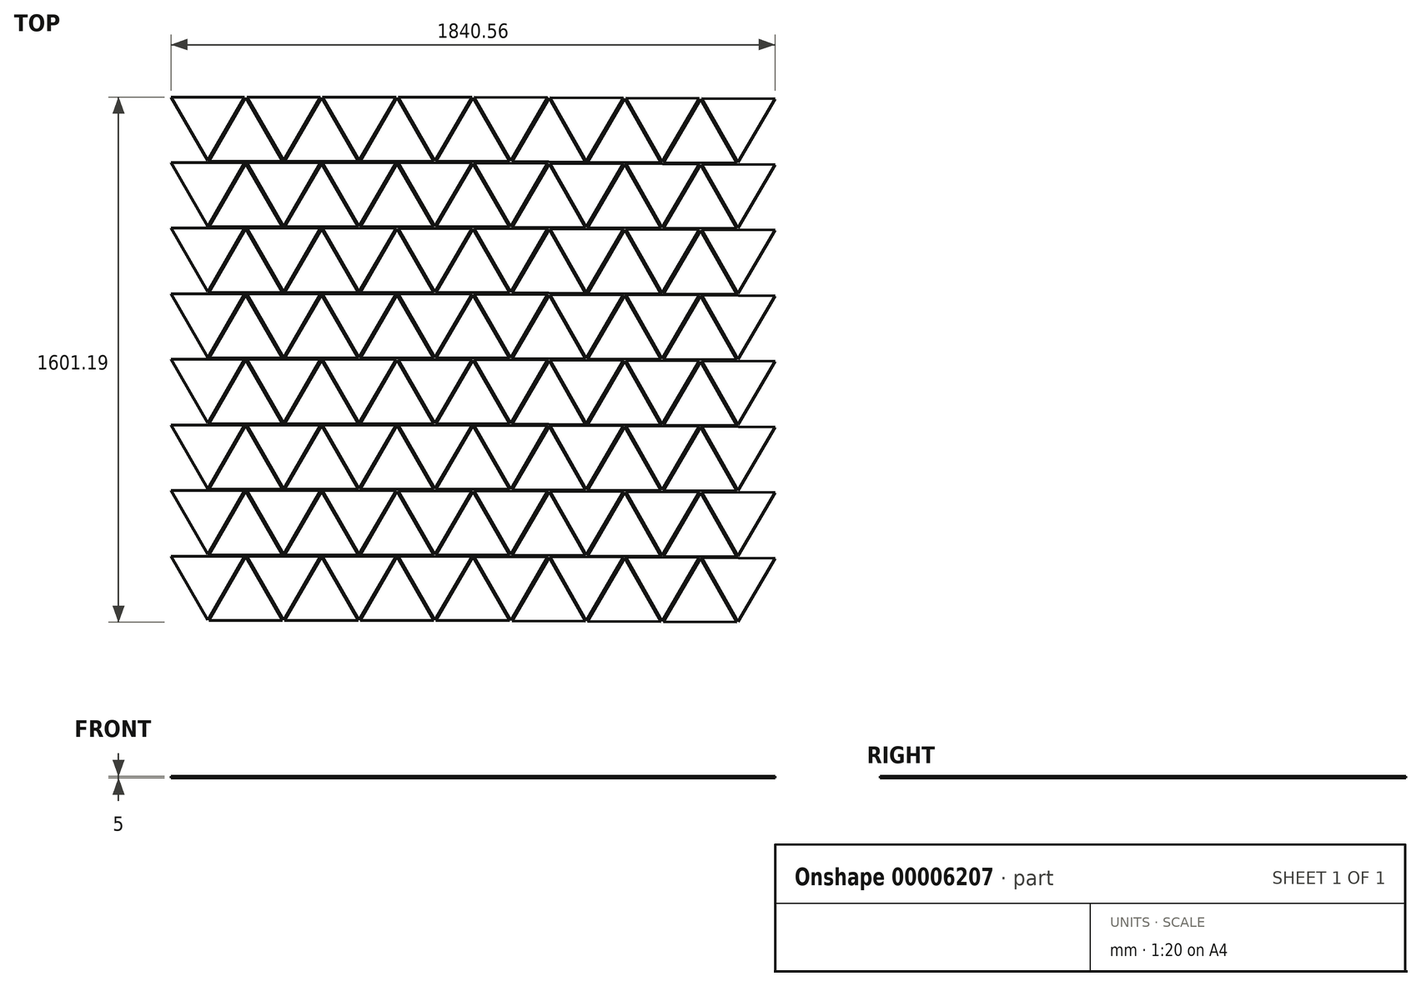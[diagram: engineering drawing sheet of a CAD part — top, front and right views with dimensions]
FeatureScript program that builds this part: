
annotation { "Feature Type Name" : "Feature", "Feature Type Description" : "" }
export const myFeature = defineFeature(function(context is Context, id is Id, definition is map)
    precondition{}
    {
        {
            var Q0;
            Q0=qCreatedBy(makeId("Top.planeOp"),FACE);
            var sketch = newSketch(context, id + "F0", { "sketchPlane" : qUnion([Q0])});
            skLineSegment(sketch, "E0.rect.bottom", {"start": v(1152.18, -1011.85) * mm, "end": v(-1150, -1011.85) * mm, "construction": true});
            skLineSegment(sketch, "E0.rect.left", {"start": v(1152.18, -1011.85) * mm, "end": v(1150, 1011.85) * mm, "construction": true});
            skLineSegment(sketch, "E0.rect.right", {"start": v(-1150, -1011.85) * mm, "end": v(-1151.84, 703.92) * mm, "construction": true});
            skPoint(sketch, "E0.rect.middle", {"position": v(0, 0) * mm});
            skCircle(sketch, "E1.cCircle", {"center": v(-1036.7, 945.18) * mm, "radius": 66.67 * mm, "construction": true});
            skLineSegment(sketch, "E1.0", {"start": v(-921.24, 1011.85) * mm, "end": v(-1036.7, 811.85) * mm, "construction": true});
            skLineSegment(sketch, "E1.1", {"start": v(-1036.7, 811.85) * mm, "end": v(-1152.18, 1011.85) * mm, "construction": true});
            skLineSegment(sketch, "E1.2", {"start": v(-1152.18, 1011.85) * mm, "end": v(-921.24, 1011.85) * mm, "construction": true});
            skPoint(sketch, "E1.0.midPoint", {"position": v(-978.97, 911.85) * mm});
            skLineSegment(sketch, "E2.0", {"start": v(-1148.71, 1009.85) * mm, "end": v(-924.7, 1009.85) * mm});
            skLineSegment(sketch, "E2.1", {"start": v(-1036.7, 815.85) * mm, "end": v(-1148.71, 1009.85) * mm});
            skLineSegment(sketch, "E2.2", {"start": v(-924.7, 1009.85) * mm, "end": v(-1036.7, 815.85) * mm});
            skLineSegment(sketch, "E3", {"start": v(-921.24, 1011.85) * mm, "end": v(-921.24, 729.24) * mm, "construction": true});
            skLineSegment(sketch, "E4.trimOffspring", {"start": v(-1151.9, 746.56) * mm, "end": v(-1152.18, 1011.85) * mm, "construction": true});
            skLineSegment(sketch, "E5.0.MirrorCS", {"start": v(-693.76, 1009.85) * mm, "end": v(-917.77, 1009.85) * mm});
            skLineSegment(sketch, "E6.0.MirrorCS", {"start": v(-917.77, 1009.85) * mm, "end": v(-805.77, 815.85) * mm});
            skLineSegment(sketch, "E7.0.MirrorCS", {"start": v(-805.77, 815.85) * mm, "end": v(-693.76, 1009.85) * mm});
            skLineSegment(sketch, "E8.0.MirrorCS", {"start": v(-690.58, 746.56) * mm, "end": v(-690.3, 1011.85) * mm, "construction": true});
            skLineSegment(sketch, "E9.0.MirrorCS", {"start": v(-575.25, 815.6) * mm, "end": v(-686.84, 1009.84) * mm});
            skLineSegment(sketch, "E10.0.MirrorCS", {"start": v(-686.84, 1009.84) * mm, "end": v(-462.82, 1009.36) * mm});
            skLineSegment(sketch, "E11.0.MirrorCS", {"start": v(-462.82, 1009.36) * mm, "end": v(-575.25, 815.6) * mm});
            skLineSegment(sketch, "E12.0.MirrorCS", {"start": v(-231.88, 1008.87) * mm, "end": v(-455.9, 1009.35) * mm});
            skLineSegment(sketch, "E13.0.MirrorCS", {"start": v(-455.9, 1009.35) * mm, "end": v(-344.3, 815.1) * mm});
            skLineSegment(sketch, "E14.0.MirrorCS", {"start": v(-344.3, 815.1) * mm, "end": v(-231.88, 1008.87) * mm});
            skLineSegment(sketch, "E15.0.MirrorCS", {"start": v(-229.27, 745.56) * mm, "end": v(-228.42, 1010.86) * mm, "construction": true});
            skLineSegment(sketch, "E16.0.MirrorCS", {"start": v(-809.23, 813.85) * mm, "end": v(-921.24, 1007.85) * mm});
            skLineSegment(sketch, "E17.0.MirrorCS", {"start": v(-1033.24, 813.85) * mm, "end": v(-809.23, 813.85) * mm});
            skLineSegment(sketch, "E18.0.MirrorCS", {"start": v(-921.24, 1007.85) * mm, "end": v(-1033.24, 813.85) * mm});
            skLineSegment(sketch, "E19", {"start": v(-805.77, 815.85) * mm, "end": v(-805.77, 688.7) * mm, "construction": true});
            skLineSegment(sketch, "E20", {"start": v(-805.77, 688.7) * mm, "end": v(-575.25, 688.7) * mm, "construction": true});
            skLineSegment(sketch, "E21", {"start": v(-575.25, 688.7) * mm, "end": v(-575.25, 815.6) * mm, "construction": true});
            skLineSegment(sketch, "E22.0.MirrorCS", {"start": v(-802.3, 813.85) * mm, "end": v(-690.3, 1007.85) * mm});
            skLineSegment(sketch, "E23.0.MirrorCS", {"start": v(-578.29, 813.85) * mm, "end": v(-802.3, 813.85) * mm});
            skLineSegment(sketch, "E24.0.MirrorCS", {"start": v(-690.3, 1007.85) * mm, "end": v(-578.29, 813.85) * mm});
            skLineSegment(sketch, "E25.0.MirrorCS", {"start": v(-460.2, 1007.85) * mm, "end": v(-572.2, 813.85) * mm});
            skLineSegment(sketch, "E26.0.MirrorCS", {"start": v(-572.2, 813.85) * mm, "end": v(-348.2, 813.85) * mm});
            skLineSegment(sketch, "E27.0.MirrorCS", {"start": v(-348.2, 813.85) * mm, "end": v(-460.2, 1007.85) * mm});
            skLineSegment(sketch, "E28.0.MirrorCS", {"start": v(-341.26, 813.85) * mm, "end": v(-229.26, 1007.85) * mm});
            skLineSegment(sketch, "E29.0.MirrorCS", {"start": v(-229.26, 1007.85) * mm, "end": v(-117.25, 813.85) * mm});
            skLineSegment(sketch, "E30.0.MirrorCS", {"start": v(-117.25, 813.85) * mm, "end": v(-341.26, 813.85) * mm});
            skLineSegment(sketch, "E31.0.MirrorCS", {"start": v(-113.8, 814.36) * mm, "end": v(-224.96, 1008.84) * mm});
            skLineSegment(sketch, "E32.0.MirrorCS", {"start": v(-224.96, 1008.84) * mm, "end": v(-0.95, 1007.88) * mm});
            skLineSegment(sketch, "E33.0.MirrorCS", {"start": v(-0.95, 1007.88) * mm, "end": v(-113.8, 814.36) * mm});
            skLineSegment(sketch, "E34.0.MirrorCS", {"start": v(-109.91, 813.08) * mm, "end": v(3.34, 1006.36) * mm});
            skLineSegment(sketch, "E35.0.MirrorCS", {"start": v(114.1, 811.64) * mm, "end": v(-109.91, 813.08) * mm});
            skLineSegment(sketch, "E36.0.MirrorCS", {"start": v(3.34, 1006.36) * mm, "end": v(114.1, 811.64) * mm});
            skLineSegment(sketch, "E37.0.MirrorCS", {"start": v(229.99, 1006.89) * mm, "end": v(5.98, 1007.85) * mm});
            skLineSegment(sketch, "E38.0.MirrorCS", {"start": v(117.15, 813.37) * mm, "end": v(229.99, 1006.89) * mm});
            skLineSegment(sketch, "E39.0.MirrorCS", {"start": v(5.98, 1007.85) * mm, "end": v(117.15, 813.37) * mm});
            skLineSegment(sketch, "E40.0.MirrorCS", {"start": v(233.43, 1004.87) * mm, "end": v(120.18, 811.6) * mm});
            skLineSegment(sketch, "E41.0.MirrorCS", {"start": v(120.18, 811.6) * mm, "end": v(344.19, 810.15) * mm});
            skLineSegment(sketch, "E42.0.MirrorCS", {"start": v(344.19, 810.15) * mm, "end": v(233.43, 1004.87) * mm});
            skLineSegment(sketch, "E43.0.MirrorCS", {"start": v(347.66, 812.13) * mm, "end": v(236.91, 1006.85) * mm});
            skLineSegment(sketch, "E44.0.MirrorCS", {"start": v(460.92, 1005.4) * mm, "end": v(347.66, 812.13) * mm});
            skLineSegment(sketch, "E45.0.MirrorCS", {"start": v(236.91, 1006.85) * mm, "end": v(460.92, 1005.4) * mm});
            skLineSegment(sketch, "E46.0.MirrorCS", {"start": v(351.11, 810.1) * mm, "end": v(464.37, 1003.38) * mm});
            skLineSegment(sketch, "E47.0.MirrorCS", {"start": v(575.12, 808.66) * mm, "end": v(351.11, 810.1) * mm});
            skLineSegment(sketch, "E48.0.MirrorCS", {"start": v(464.37, 1003.38) * mm, "end": v(575.12, 808.66) * mm});
            skLineSegment(sketch, "E49.0.MirrorCS", {"start": v(467.85, 1005.36) * mm, "end": v(578.6, 810.64) * mm});
            skLineSegment(sketch, "E50.0.MirrorCS", {"start": v(691.85, 1003.91) * mm, "end": v(467.85, 1005.36) * mm});
            skLineSegment(sketch, "E51.0.MirrorCS", {"start": v(578.6, 810.64) * mm, "end": v(691.85, 1003.91) * mm});
            skLineSegment(sketch, "E52", {"start": v(578.6, 810.64) * mm, "end": v(579.85, 1004.64) * mm, "construction": true});
            skLineSegment(sketch, "E53", {"start": v(-1036.7, 811.85) * mm, "end": v(-1131.82, 811.85) * mm, "construction": true});
            skLineSegment(sketch, "E54.0.1.0", {"start": v(229.99, 806.89) * mm, "end": v(5.98, 807.85) * mm});
            skLineSegment(sketch, "E54.0.1.1", {"start": v(-462.82, 809.36) * mm, "end": v(-575.25, 615.6) * mm});
            skLineSegment(sketch, "E54.0.1.2", {"start": v(-348.2, 613.85) * mm, "end": v(-460.2, 807.85) * mm});
            skLineSegment(sketch, "E54.0.1.3", {"start": v(347.66, 612.13) * mm, "end": v(236.91, 806.85) * mm});
            skLineSegment(sketch, "E54.0.1.4", {"start": v(233.43, 804.87) * mm, "end": v(120.18, 611.6) * mm});
            skLineSegment(sketch, "E54.0.1.5", {"start": v(-690.3, 807.85) * mm, "end": v(-578.29, 613.85) * mm});
            skLineSegment(sketch, "E54.0.1.6", {"start": v(-917.77, 809.85) * mm, "end": v(-805.77, 615.85) * mm});
            skLineSegment(sketch, "E54.0.1.7", {"start": v(-805.77, 615.85) * mm, "end": v(-693.76, 809.85) * mm});
            skLineSegment(sketch, "E54.0.1.8", {"start": v(-117.25, 613.85) * mm, "end": v(-341.26, 613.85) * mm});
            skLineSegment(sketch, "E54.0.1.9", {"start": v(351.11, 610.1) * mm, "end": v(464.37, 803.38) * mm});
            skLineSegment(sketch, "E54.0.1.10", {"start": v(-344.3, 615.1) * mm, "end": v(-231.88, 808.87) * mm});
            skLineSegment(sketch, "E54.0.1.11", {"start": v(-1033.24, 613.85) * mm, "end": v(-809.23, 613.85) * mm});
            skLineSegment(sketch, "E54.0.1.12", {"start": v(467.85, 805.36) * mm, "end": v(578.6, 610.64) * mm});
            skLineSegment(sketch, "E54.0.1.13", {"start": v(-0.95, 807.88) * mm, "end": v(-113.8, 614.36) * mm});
            skLineSegment(sketch, "E54.0.1.14", {"start": v(-686.84, 809.84) * mm, "end": v(-462.82, 809.36) * mm});
            skLineSegment(sketch, "E54.0.1.15", {"start": v(-693.76, 809.85) * mm, "end": v(-917.77, 809.85) * mm});
            skLineSegment(sketch, "E54.0.1.16", {"start": v(-924.7, 809.85) * mm, "end": v(-1036.7, 615.85) * mm});
            skLineSegment(sketch, "E54.0.1.17", {"start": v(344.19, 610.15) * mm, "end": v(233.43, 804.87) * mm});
            skLineSegment(sketch, "E54.0.1.18", {"start": v(-572.2, 613.85) * mm, "end": v(-348.2, 613.85) * mm});
            skLineSegment(sketch, "E54.0.1.19", {"start": v(-1148.71, 809.85) * mm, "end": v(-924.7, 809.85) * mm});
            skLineSegment(sketch, "E54.0.1.20", {"start": v(-1036.7, 615.85) * mm, "end": v(-1148.71, 809.85) * mm});
            skLineSegment(sketch, "E54.0.1.21", {"start": v(-578.29, 613.85) * mm, "end": v(-802.3, 613.85) * mm});
            skLineSegment(sketch, "E54.0.1.22", {"start": v(5.98, 807.85) * mm, "end": v(117.15, 613.37) * mm});
            skLineSegment(sketch, "E54.0.1.23", {"start": v(575.12, 608.66) * mm, "end": v(351.11, 610.1) * mm});
            skLineSegment(sketch, "E54.0.1.24", {"start": v(-113.8, 614.36) * mm, "end": v(-224.96, 808.84) * mm});
            skLineSegment(sketch, "E54.0.1.25", {"start": v(-921.24, 807.85) * mm, "end": v(-1033.24, 613.85) * mm});
            skLineSegment(sketch, "E54.0.1.26", {"start": v(-109.91, 613.08) * mm, "end": v(3.34, 806.36) * mm});
            skLineSegment(sketch, "E54.0.1.27", {"start": v(691.85, 803.91) * mm, "end": v(467.85, 805.36) * mm});
            skLineSegment(sketch, "E54.0.1.28", {"start": v(-575.25, 615.6) * mm, "end": v(-686.84, 809.84) * mm});
            skLineSegment(sketch, "E54.0.1.29", {"start": v(-460.2, 807.85) * mm, "end": v(-572.2, 613.85) * mm});
            skLineSegment(sketch, "E54.0.1.30", {"start": v(120.18, 611.6) * mm, "end": v(344.19, 610.15) * mm});
            skLineSegment(sketch, "E54.0.1.31", {"start": v(114.1, 611.64) * mm, "end": v(-109.91, 613.08) * mm});
            skLineSegment(sketch, "E54.0.1.32", {"start": v(578.6, 610.64) * mm, "end": v(691.85, 803.91) * mm});
            skLineSegment(sketch, "E54.0.1.33", {"start": v(117.15, 613.37) * mm, "end": v(229.99, 806.89) * mm});
            skPoint(sketch, "E54.0.1.34", {"position": v(-978.97, 711.85) * mm});
            skLineSegment(sketch, "E54.0.1.35", {"start": v(-802.3, 613.85) * mm, "end": v(-690.3, 807.85) * mm});
            skLineSegment(sketch, "E54.0.1.36", {"start": v(460.92, 805.4) * mm, "end": v(347.66, 612.13) * mm});
            skLineSegment(sketch, "E54.0.1.37", {"start": v(-341.26, 613.85) * mm, "end": v(-229.26, 807.85) * mm});
            skLineSegment(sketch, "E54.0.1.38", {"start": v(-231.88, 808.87) * mm, "end": v(-455.9, 809.35) * mm});
            skLineSegment(sketch, "E54.0.1.39", {"start": v(578.6, 610.64) * mm, "end": v(579.85, 804.64) * mm, "construction": true});
            skLineSegment(sketch, "E54.0.1.40", {"start": v(3.34, 806.36) * mm, "end": v(114.1, 611.64) * mm});
            skLineSegment(sketch, "E54.0.1.41", {"start": v(464.37, 803.38) * mm, "end": v(575.12, 608.66) * mm});
            skLineSegment(sketch, "E54.0.1.42", {"start": v(-224.96, 808.84) * mm, "end": v(-0.95, 807.88) * mm});
            skLineSegment(sketch, "E54.0.1.43", {"start": v(-809.23, 613.85) * mm, "end": v(-921.24, 807.85) * mm});
            skLineSegment(sketch, "E54.0.1.44", {"start": v(236.91, 806.85) * mm, "end": v(460.92, 805.4) * mm});
            skLineSegment(sketch, "E54.0.1.45", {"start": v(-229.26, 807.85) * mm, "end": v(-117.25, 613.85) * mm});
            skLineSegment(sketch, "E54.0.1.46", {"start": v(-455.9, 809.35) * mm, "end": v(-344.3, 615.1) * mm});
            skLineSegment(sketch, "E54.0.2.0", {"start": v(229.99, 606.89) * mm, "end": v(5.98, 607.85) * mm});
            skLineSegment(sketch, "E54.0.2.1", {"start": v(-462.82, 609.36) * mm, "end": v(-575.25, 415.6) * mm});
            skLineSegment(sketch, "E54.0.2.2", {"start": v(-348.2, 413.85) * mm, "end": v(-460.2, 607.85) * mm});
            skLineSegment(sketch, "E54.0.2.3", {"start": v(347.66, 412.13) * mm, "end": v(236.91, 606.85) * mm});
            skLineSegment(sketch, "E54.0.2.4", {"start": v(233.43, 604.87) * mm, "end": v(120.18, 411.6) * mm});
            skLineSegment(sketch, "E54.0.2.5", {"start": v(-690.3, 607.85) * mm, "end": v(-578.29, 413.85) * mm});
            skLineSegment(sketch, "E54.0.2.6", {"start": v(-917.77, 609.85) * mm, "end": v(-805.77, 415.85) * mm});
            skLineSegment(sketch, "E54.0.2.7", {"start": v(-805.77, 415.85) * mm, "end": v(-693.76, 609.85) * mm});
            skLineSegment(sketch, "E54.0.2.8", {"start": v(-117.25, 413.85) * mm, "end": v(-341.26, 413.85) * mm});
            skLineSegment(sketch, "E54.0.2.9", {"start": v(351.11, 410.1) * mm, "end": v(464.37, 603.38) * mm});
            skLineSegment(sketch, "E54.0.2.10", {"start": v(-344.3, 415.1) * mm, "end": v(-231.88, 608.87) * mm});
            skLineSegment(sketch, "E54.0.2.11", {"start": v(-1033.24, 413.85) * mm, "end": v(-809.23, 413.85) * mm});
            skLineSegment(sketch, "E54.0.2.12", {"start": v(467.85, 605.36) * mm, "end": v(578.6, 410.64) * mm});
            skLineSegment(sketch, "E54.0.2.13", {"start": v(-0.95, 607.88) * mm, "end": v(-113.8, 414.36) * mm});
            skLineSegment(sketch, "E54.0.2.14", {"start": v(-686.84, 609.84) * mm, "end": v(-462.82, 609.36) * mm});
            skLineSegment(sketch, "E54.0.2.15", {"start": v(-693.76, 609.85) * mm, "end": v(-917.77, 609.85) * mm});
            skLineSegment(sketch, "E54.0.2.16", {"start": v(-924.7, 609.85) * mm, "end": v(-1036.7, 415.85) * mm});
            skLineSegment(sketch, "E54.0.2.17", {"start": v(344.19, 410.15) * mm, "end": v(233.43, 604.87) * mm});
            skLineSegment(sketch, "E54.0.2.18", {"start": v(-572.2, 413.85) * mm, "end": v(-348.2, 413.85) * mm});
            skLineSegment(sketch, "E54.0.2.19", {"start": v(-1148.71, 609.85) * mm, "end": v(-924.7, 609.85) * mm});
            skLineSegment(sketch, "E54.0.2.20", {"start": v(-1036.7, 415.85) * mm, "end": v(-1148.71, 609.85) * mm});
            skLineSegment(sketch, "E54.0.2.21", {"start": v(-578.29, 413.85) * mm, "end": v(-802.3, 413.85) * mm});
            skLineSegment(sketch, "E54.0.2.22", {"start": v(5.98, 607.85) * mm, "end": v(117.15, 413.37) * mm});
            skLineSegment(sketch, "E54.0.2.23", {"start": v(575.12, 408.66) * mm, "end": v(351.11, 410.1) * mm});
            skLineSegment(sketch, "E54.0.2.24", {"start": v(-113.8, 414.36) * mm, "end": v(-224.96, 608.84) * mm});
            skLineSegment(sketch, "E54.0.2.25", {"start": v(-921.24, 607.85) * mm, "end": v(-1033.24, 413.85) * mm});
            skLineSegment(sketch, "E54.0.2.26", {"start": v(-109.91, 413.08) * mm, "end": v(3.34, 606.36) * mm});
            skLineSegment(sketch, "E54.0.2.27", {"start": v(691.85, 603.91) * mm, "end": v(467.85, 605.36) * mm});
            skLineSegment(sketch, "E54.0.2.28", {"start": v(-575.25, 415.6) * mm, "end": v(-686.84, 609.84) * mm});
            skLineSegment(sketch, "E54.0.2.29", {"start": v(-460.2, 607.85) * mm, "end": v(-572.2, 413.85) * mm});
            skLineSegment(sketch, "E54.0.2.30", {"start": v(120.18, 411.6) * mm, "end": v(344.19, 410.15) * mm});
            skLineSegment(sketch, "E54.0.2.31", {"start": v(114.1, 411.64) * mm, "end": v(-109.91, 413.08) * mm});
            skLineSegment(sketch, "E54.0.2.32", {"start": v(578.6, 410.64) * mm, "end": v(691.85, 603.91) * mm});
            skLineSegment(sketch, "E54.0.2.33", {"start": v(117.15, 413.37) * mm, "end": v(229.99, 606.89) * mm});
            skPoint(sketch, "E54.0.2.34", {"position": v(-978.97, 511.85) * mm});
            skLineSegment(sketch, "E54.0.2.35", {"start": v(-802.3, 413.85) * mm, "end": v(-690.3, 607.85) * mm});
            skLineSegment(sketch, "E54.0.2.36", {"start": v(460.92, 605.4) * mm, "end": v(347.66, 412.13) * mm});
            skLineSegment(sketch, "E54.0.2.37", {"start": v(-341.26, 413.85) * mm, "end": v(-229.26, 607.85) * mm});
            skLineSegment(sketch, "E54.0.2.38", {"start": v(-231.88, 608.87) * mm, "end": v(-455.9, 609.35) * mm});
            skLineSegment(sketch, "E54.0.2.39", {"start": v(578.6, 410.64) * mm, "end": v(579.85, 604.64) * mm, "construction": true});
            skLineSegment(sketch, "E54.0.2.40", {"start": v(3.34, 606.36) * mm, "end": v(114.1, 411.64) * mm});
            skLineSegment(sketch, "E54.0.2.41", {"start": v(464.37, 603.38) * mm, "end": v(575.12, 408.66) * mm});
            skLineSegment(sketch, "E54.0.2.42", {"start": v(-224.96, 608.84) * mm, "end": v(-0.95, 607.88) * mm});
            skLineSegment(sketch, "E54.0.2.43", {"start": v(-809.23, 413.85) * mm, "end": v(-921.24, 607.85) * mm});
            skLineSegment(sketch, "E54.0.2.44", {"start": v(236.91, 606.85) * mm, "end": v(460.92, 605.4) * mm});
            skLineSegment(sketch, "E54.0.2.45", {"start": v(-229.26, 607.85) * mm, "end": v(-117.25, 413.85) * mm});
            skLineSegment(sketch, "E54.0.2.46", {"start": v(-455.9, 609.35) * mm, "end": v(-344.3, 415.1) * mm});
            skLineSegment(sketch, "E54.0.3.0", {"start": v(229.99, 406.89) * mm, "end": v(5.98, 407.85) * mm});
            skLineSegment(sketch, "E54.0.3.1", {"start": v(-462.82, 409.36) * mm, "end": v(-575.25, 215.6) * mm});
            skLineSegment(sketch, "E54.0.3.2", {"start": v(-348.2, 213.85) * mm, "end": v(-460.2, 407.85) * mm});
            skLineSegment(sketch, "E54.0.3.3", {"start": v(347.66, 212.13) * mm, "end": v(236.91, 406.85) * mm});
            skLineSegment(sketch, "E54.0.3.4", {"start": v(233.43, 404.87) * mm, "end": v(120.18, 211.6) * mm});
            skLineSegment(sketch, "E54.0.3.5", {"start": v(-690.3, 407.85) * mm, "end": v(-578.29, 213.85) * mm});
            skLineSegment(sketch, "E54.0.3.6", {"start": v(-917.77, 409.85) * mm, "end": v(-805.77, 215.85) * mm});
            skLineSegment(sketch, "E54.0.3.7", {"start": v(-805.77, 215.85) * mm, "end": v(-693.76, 409.85) * mm});
            skLineSegment(sketch, "E54.0.3.8", {"start": v(-117.25, 213.85) * mm, "end": v(-341.26, 213.85) * mm});
            skLineSegment(sketch, "E54.0.3.9", {"start": v(351.11, 210.1) * mm, "end": v(464.37, 403.38) * mm});
            skLineSegment(sketch, "E54.0.3.10", {"start": v(-344.3, 215.1) * mm, "end": v(-231.88, 408.87) * mm});
            skLineSegment(sketch, "E54.0.3.11", {"start": v(-1033.24, 213.85) * mm, "end": v(-809.23, 213.85) * mm});
            skLineSegment(sketch, "E54.0.3.12", {"start": v(467.85, 405.36) * mm, "end": v(578.6, 210.64) * mm});
            skLineSegment(sketch, "E54.0.3.13", {"start": v(-0.95, 407.88) * mm, "end": v(-113.8, 214.36) * mm});
            skLineSegment(sketch, "E54.0.3.14", {"start": v(-686.84, 409.84) * mm, "end": v(-462.82, 409.36) * mm});
            skLineSegment(sketch, "E54.0.3.15", {"start": v(-693.76, 409.85) * mm, "end": v(-917.77, 409.85) * mm});
            skLineSegment(sketch, "E54.0.3.16", {"start": v(-924.7, 409.85) * mm, "end": v(-1036.7, 215.85) * mm});
            skLineSegment(sketch, "E54.0.3.17", {"start": v(344.19, 210.15) * mm, "end": v(233.43, 404.87) * mm});
            skLineSegment(sketch, "E54.0.3.18", {"start": v(-572.2, 213.85) * mm, "end": v(-348.2, 213.85) * mm});
            skLineSegment(sketch, "E54.0.3.19", {"start": v(-1148.71, 409.85) * mm, "end": v(-924.7, 409.85) * mm});
            skLineSegment(sketch, "E54.0.3.20", {"start": v(-1036.7, 215.85) * mm, "end": v(-1148.71, 409.85) * mm});
            skLineSegment(sketch, "E54.0.3.21", {"start": v(-578.29, 213.85) * mm, "end": v(-802.3, 213.85) * mm});
            skLineSegment(sketch, "E54.0.3.22", {"start": v(5.98, 407.85) * mm, "end": v(117.15, 213.37) * mm});
            skLineSegment(sketch, "E54.0.3.23", {"start": v(575.12, 208.66) * mm, "end": v(351.11, 210.1) * mm});
            skLineSegment(sketch, "E54.0.3.24", {"start": v(-113.8, 214.36) * mm, "end": v(-224.96, 408.84) * mm});
            skLineSegment(sketch, "E54.0.3.25", {"start": v(-921.24, 407.85) * mm, "end": v(-1033.24, 213.85) * mm});
            skLineSegment(sketch, "E54.0.3.26", {"start": v(-109.91, 213.08) * mm, "end": v(3.34, 406.36) * mm});
            skLineSegment(sketch, "E54.0.3.27", {"start": v(691.85, 403.91) * mm, "end": v(467.85, 405.36) * mm});
            skLineSegment(sketch, "E54.0.3.28", {"start": v(-575.25, 215.6) * mm, "end": v(-686.84, 409.84) * mm});
            skLineSegment(sketch, "E54.0.3.29", {"start": v(-460.2, 407.85) * mm, "end": v(-572.2, 213.85) * mm});
            skLineSegment(sketch, "E54.0.3.30", {"start": v(120.18, 211.6) * mm, "end": v(344.19, 210.15) * mm});
            skLineSegment(sketch, "E54.0.3.31", {"start": v(114.1, 211.64) * mm, "end": v(-109.91, 213.08) * mm});
            skLineSegment(sketch, "E54.0.3.32", {"start": v(578.6, 210.64) * mm, "end": v(691.85, 403.91) * mm});
            skLineSegment(sketch, "E54.0.3.33", {"start": v(117.15, 213.37) * mm, "end": v(229.99, 406.89) * mm});
            skPoint(sketch, "E54.0.3.34", {"position": v(-978.97, 311.85) * mm});
            skLineSegment(sketch, "E54.0.3.35", {"start": v(-802.3, 213.85) * mm, "end": v(-690.3, 407.85) * mm});
            skLineSegment(sketch, "E54.0.3.36", {"start": v(460.92, 405.4) * mm, "end": v(347.66, 212.13) * mm});
            skLineSegment(sketch, "E54.0.3.37", {"start": v(-341.26, 213.85) * mm, "end": v(-229.26, 407.85) * mm});
            skLineSegment(sketch, "E54.0.3.38", {"start": v(-231.88, 408.87) * mm, "end": v(-455.9, 409.35) * mm});
            skLineSegment(sketch, "E54.0.3.39", {"start": v(578.6, 210.64) * mm, "end": v(579.85, 404.64) * mm, "construction": true});
            skLineSegment(sketch, "E54.0.3.40", {"start": v(3.34, 406.36) * mm, "end": v(114.1, 211.64) * mm});
            skLineSegment(sketch, "E54.0.3.41", {"start": v(464.37, 403.38) * mm, "end": v(575.12, 208.66) * mm});
            skLineSegment(sketch, "E54.0.3.42", {"start": v(-224.96, 408.84) * mm, "end": v(-0.95, 407.88) * mm});
            skLineSegment(sketch, "E54.0.3.43", {"start": v(-809.23, 213.85) * mm, "end": v(-921.24, 407.85) * mm});
            skLineSegment(sketch, "E54.0.3.44", {"start": v(236.91, 406.85) * mm, "end": v(460.92, 405.4) * mm});
            skLineSegment(sketch, "E54.0.3.45", {"start": v(-229.26, 407.85) * mm, "end": v(-117.25, 213.85) * mm});
            skLineSegment(sketch, "E54.0.3.46", {"start": v(-455.9, 409.35) * mm, "end": v(-344.3, 215.1) * mm});
            skLineSegment(sketch, "E54.0.4.0", {"start": v(229.99, 206.89) * mm, "end": v(5.98, 207.85) * mm});
            skLineSegment(sketch, "E54.0.4.1", {"start": v(-462.82, 209.36) * mm, "end": v(-575.25, 15.6) * mm});
            skLineSegment(sketch, "E54.0.4.2", {"start": v(-348.2, 13.85) * mm, "end": v(-460.2, 207.85) * mm});
            skLineSegment(sketch, "E54.0.4.3", {"start": v(347.66, 12.13) * mm, "end": v(236.91, 206.85) * mm});
            skLineSegment(sketch, "E54.0.4.4", {"start": v(233.43, 204.87) * mm, "end": v(120.18, 11.6) * mm});
            skLineSegment(sketch, "E54.0.4.5", {"start": v(-690.3, 207.85) * mm, "end": v(-578.29, 13.85) * mm});
            skLineSegment(sketch, "E54.0.4.6", {"start": v(-917.77, 209.85) * mm, "end": v(-805.77, 15.85) * mm});
            skLineSegment(sketch, "E54.0.4.7", {"start": v(-805.77, 15.85) * mm, "end": v(-693.76, 209.85) * mm});
            skLineSegment(sketch, "E54.0.4.8", {"start": v(-117.25, 13.85) * mm, "end": v(-341.26, 13.85) * mm});
            skLineSegment(sketch, "E54.0.4.9", {"start": v(351.11, 10.1) * mm, "end": v(464.37, 203.38) * mm});
            skLineSegment(sketch, "E54.0.4.10", {"start": v(-344.3, 15.1) * mm, "end": v(-231.88, 208.87) * mm});
            skLineSegment(sketch, "E54.0.4.11", {"start": v(-1033.24, 13.85) * mm, "end": v(-809.23, 13.85) * mm});
            skLineSegment(sketch, "E54.0.4.12", {"start": v(467.85, 205.36) * mm, "end": v(578.6, 10.64) * mm});
            skLineSegment(sketch, "E54.0.4.13", {"start": v(-0.95, 207.88) * mm, "end": v(-113.8, 14.36) * mm});
            skLineSegment(sketch, "E54.0.4.14", {"start": v(-686.84, 209.84) * mm, "end": v(-462.82, 209.36) * mm});
            skLineSegment(sketch, "E54.0.4.15", {"start": v(-693.76, 209.85) * mm, "end": v(-917.77, 209.85) * mm});
            skLineSegment(sketch, "E54.0.4.16", {"start": v(-924.7, 209.85) * mm, "end": v(-1036.7, 15.85) * mm});
            skLineSegment(sketch, "E54.0.4.17", {"start": v(344.19, 10.15) * mm, "end": v(233.43, 204.87) * mm});
            skLineSegment(sketch, "E54.0.4.18", {"start": v(-572.2, 13.85) * mm, "end": v(-348.2, 13.85) * mm});
            skLineSegment(sketch, "E54.0.4.19", {"start": v(-1148.71, 209.85) * mm, "end": v(-924.7, 209.85) * mm});
            skLineSegment(sketch, "E54.0.4.20", {"start": v(-1036.7, 15.85) * mm, "end": v(-1148.71, 209.85) * mm});
            skLineSegment(sketch, "E54.0.4.21", {"start": v(-578.29, 13.85) * mm, "end": v(-802.3, 13.85) * mm});
            skLineSegment(sketch, "E54.0.4.22", {"start": v(5.98, 207.85) * mm, "end": v(117.15, 13.37) * mm});
            skLineSegment(sketch, "E54.0.4.23", {"start": v(575.12, 8.66) * mm, "end": v(351.11, 10.1) * mm});
            skLineSegment(sketch, "E54.0.4.24", {"start": v(-113.8, 14.36) * mm, "end": v(-224.96, 208.84) * mm});
            skLineSegment(sketch, "E54.0.4.25", {"start": v(-921.24, 207.85) * mm, "end": v(-1033.24, 13.85) * mm});
            skLineSegment(sketch, "E54.0.4.26", {"start": v(-109.91, 13.08) * mm, "end": v(3.34, 206.36) * mm});
            skLineSegment(sketch, "E54.0.4.27", {"start": v(691.85, 203.91) * mm, "end": v(467.85, 205.36) * mm});
            skLineSegment(sketch, "E54.0.4.28", {"start": v(-575.25, 15.6) * mm, "end": v(-686.84, 209.84) * mm});
            skLineSegment(sketch, "E54.0.4.29", {"start": v(-460.2, 207.85) * mm, "end": v(-572.2, 13.85) * mm});
            skLineSegment(sketch, "E54.0.4.30", {"start": v(120.18, 11.6) * mm, "end": v(344.19, 10.15) * mm});
            skLineSegment(sketch, "E54.0.4.31", {"start": v(114.1, 11.64) * mm, "end": v(-109.91, 13.08) * mm});
            skLineSegment(sketch, "E54.0.4.32", {"start": v(578.6, 10.64) * mm, "end": v(691.85, 203.91) * mm});
            skLineSegment(sketch, "E54.0.4.33", {"start": v(117.15, 13.37) * mm, "end": v(229.99, 206.89) * mm});
            skPoint(sketch, "E54.0.4.34", {"position": v(-978.97, 111.85) * mm});
            skLineSegment(sketch, "E54.0.4.35", {"start": v(-802.3, 13.85) * mm, "end": v(-690.3, 207.85) * mm});
            skLineSegment(sketch, "E54.0.4.36", {"start": v(460.92, 205.4) * mm, "end": v(347.66, 12.13) * mm});
            skLineSegment(sketch, "E54.0.4.37", {"start": v(-341.26, 13.85) * mm, "end": v(-229.26, 207.85) * mm});
            skLineSegment(sketch, "E54.0.4.38", {"start": v(-231.88, 208.87) * mm, "end": v(-455.9, 209.35) * mm});
            skLineSegment(sketch, "E54.0.4.39", {"start": v(578.6, 10.64) * mm, "end": v(579.85, 204.64) * mm, "construction": true});
            skLineSegment(sketch, "E54.0.4.40", {"start": v(3.34, 206.36) * mm, "end": v(114.1, 11.64) * mm});
            skLineSegment(sketch, "E54.0.4.41", {"start": v(464.37, 203.38) * mm, "end": v(575.12, 8.66) * mm});
            skLineSegment(sketch, "E54.0.4.42", {"start": v(-224.96, 208.84) * mm, "end": v(-0.95, 207.88) * mm});
            skLineSegment(sketch, "E54.0.4.43", {"start": v(-809.23, 13.85) * mm, "end": v(-921.24, 207.85) * mm});
            skLineSegment(sketch, "E54.0.4.44", {"start": v(236.91, 206.85) * mm, "end": v(460.92, 205.4) * mm});
            skLineSegment(sketch, "E54.0.4.45", {"start": v(-229.26, 207.85) * mm, "end": v(-117.25, 13.85) * mm});
            skLineSegment(sketch, "E54.0.4.46", {"start": v(-455.9, 209.35) * mm, "end": v(-344.3, 15.1) * mm});
            skLineSegment(sketch, "E54.0.5.0", {"start": v(229.99, 6.89) * mm, "end": v(5.98, 7.85) * mm});
            skLineSegment(sketch, "E54.0.5.1", {"start": v(-462.82, 9.36) * mm, "end": v(-575.25, -184.4) * mm});
            skLineSegment(sketch, "E54.0.5.2", {"start": v(-348.2, -186.15) * mm, "end": v(-460.2, 7.85) * mm});
            skLineSegment(sketch, "E54.0.5.3", {"start": v(347.66, -187.87) * mm, "end": v(236.91, 6.85) * mm});
            skLineSegment(sketch, "E54.0.5.4", {"start": v(233.43, 4.87) * mm, "end": v(120.18, -188.4) * mm});
            skLineSegment(sketch, "E54.0.5.5", {"start": v(-690.3, 7.85) * mm, "end": v(-578.29, -186.15) * mm});
            skLineSegment(sketch, "E54.0.5.6", {"start": v(-917.77, 9.85) * mm, "end": v(-805.77, -184.15) * mm});
            skLineSegment(sketch, "E54.0.5.7", {"start": v(-805.77, -184.15) * mm, "end": v(-693.76, 9.85) * mm});
            skLineSegment(sketch, "E54.0.5.8", {"start": v(-117.25, -186.15) * mm, "end": v(-341.26, -186.15) * mm});
            skLineSegment(sketch, "E54.0.5.9", {"start": v(351.11, -189.9) * mm, "end": v(464.37, 3.38) * mm});
            skLineSegment(sketch, "E54.0.5.10", {"start": v(-344.3, -184.9) * mm, "end": v(-231.88, 8.87) * mm});
            skLineSegment(sketch, "E54.0.5.11", {"start": v(-1033.24, -186.15) * mm, "end": v(-809.23, -186.15) * mm});
            skLineSegment(sketch, "E54.0.5.12", {"start": v(467.85, 5.36) * mm, "end": v(578.6, -189.36) * mm});
            skLineSegment(sketch, "E54.0.5.13", {"start": v(-0.95, 7.88) * mm, "end": v(-113.8, -185.64) * mm});
            skLineSegment(sketch, "E54.0.5.14", {"start": v(-686.84, 9.84) * mm, "end": v(-462.82, 9.36) * mm});
            skLineSegment(sketch, "E54.0.5.15", {"start": v(-693.76, 9.85) * mm, "end": v(-917.77, 9.85) * mm});
            skLineSegment(sketch, "E54.0.5.16", {"start": v(-924.7, 9.85) * mm, "end": v(-1036.7, -184.15) * mm});
            skLineSegment(sketch, "E54.0.5.17", {"start": v(344.19, -189.85) * mm, "end": v(233.43, 4.87) * mm});
            skLineSegment(sketch, "E54.0.5.18", {"start": v(-572.2, -186.15) * mm, "end": v(-348.2, -186.15) * mm});
            skLineSegment(sketch, "E54.0.5.19", {"start": v(-1148.71, 9.85) * mm, "end": v(-924.7, 9.85) * mm});
            skLineSegment(sketch, "E54.0.5.20", {"start": v(-1036.7, -184.15) * mm, "end": v(-1148.71, 9.85) * mm});
            skLineSegment(sketch, "E54.0.5.21", {"start": v(-578.29, -186.15) * mm, "end": v(-802.3, -186.15) * mm});
            skLineSegment(sketch, "E54.0.5.22", {"start": v(5.98, 7.85) * mm, "end": v(117.15, -186.63) * mm});
            skLineSegment(sketch, "E54.0.5.23", {"start": v(575.12, -191.34) * mm, "end": v(351.11, -189.9) * mm});
            skLineSegment(sketch, "E54.0.5.24", {"start": v(-113.8, -185.64) * mm, "end": v(-224.96, 8.84) * mm});
            skLineSegment(sketch, "E54.0.5.25", {"start": v(-921.24, 7.85) * mm, "end": v(-1033.24, -186.15) * mm});
            skLineSegment(sketch, "E54.0.5.26", {"start": v(-109.91, -186.92) * mm, "end": v(3.34, 6.36) * mm});
            skLineSegment(sketch, "E54.0.5.27", {"start": v(691.85, 3.91) * mm, "end": v(467.85, 5.36) * mm});
            skLineSegment(sketch, "E54.0.5.28", {"start": v(-575.25, -184.4) * mm, "end": v(-686.84, 9.84) * mm});
            skLineSegment(sketch, "E54.0.5.29", {"start": v(-460.2, 7.85) * mm, "end": v(-572.2, -186.15) * mm});
            skLineSegment(sketch, "E54.0.5.30", {"start": v(120.18, -188.4) * mm, "end": v(344.19, -189.85) * mm});
            skLineSegment(sketch, "E54.0.5.31", {"start": v(114.1, -188.36) * mm, "end": v(-109.91, -186.92) * mm});
            skLineSegment(sketch, "E54.0.5.32", {"start": v(578.6, -189.36) * mm, "end": v(691.85, 3.91) * mm});
            skLineSegment(sketch, "E54.0.5.33", {"start": v(117.15, -186.63) * mm, "end": v(229.99, 6.89) * mm});
            skPoint(sketch, "E54.0.5.34", {"position": v(-978.97, -88.15) * mm});
            skLineSegment(sketch, "E54.0.5.35", {"start": v(-802.3, -186.15) * mm, "end": v(-690.3, 7.85) * mm});
            skLineSegment(sketch, "E54.0.5.36", {"start": v(460.92, 5.4) * mm, "end": v(347.66, -187.87) * mm});
            skLineSegment(sketch, "E54.0.5.37", {"start": v(-341.26, -186.15) * mm, "end": v(-229.26, 7.85) * mm});
            skLineSegment(sketch, "E54.0.5.38", {"start": v(-231.88, 8.87) * mm, "end": v(-455.9, 9.35) * mm});
            skLineSegment(sketch, "E54.0.5.39", {"start": v(578.6, -189.36) * mm, "end": v(579.85, 4.64) * mm, "construction": true});
            skLineSegment(sketch, "E54.0.5.40", {"start": v(3.34, 6.36) * mm, "end": v(114.1, -188.36) * mm});
            skLineSegment(sketch, "E54.0.5.41", {"start": v(464.37, 3.38) * mm, "end": v(575.12, -191.34) * mm});
            skLineSegment(sketch, "E54.0.5.42", {"start": v(-224.96, 8.84) * mm, "end": v(-0.95, 7.88) * mm});
            skLineSegment(sketch, "E54.0.5.43", {"start": v(-809.23, -186.15) * mm, "end": v(-921.24, 7.85) * mm});
            skLineSegment(sketch, "E54.0.5.44", {"start": v(236.91, 6.85) * mm, "end": v(460.92, 5.4) * mm});
            skLineSegment(sketch, "E54.0.5.45", {"start": v(-229.26, 7.85) * mm, "end": v(-117.25, -186.15) * mm});
            skLineSegment(sketch, "E54.0.5.46", {"start": v(-455.9, 9.35) * mm, "end": v(-344.3, -184.9) * mm});
            skLineSegment(sketch, "E54.0.6.0", {"start": v(229.99, -193.11) * mm, "end": v(5.98, -192.15) * mm});
            skLineSegment(sketch, "E54.0.6.1", {"start": v(-462.82, -190.64) * mm, "end": v(-575.25, -384.4) * mm});
            skLineSegment(sketch, "E54.0.6.2", {"start": v(-348.2, -386.15) * mm, "end": v(-460.2, -192.15) * mm});
            skLineSegment(sketch, "E54.0.6.3", {"start": v(347.66, -387.87) * mm, "end": v(236.91, -193.15) * mm});
            skLineSegment(sketch, "E54.0.6.4", {"start": v(233.43, -195.13) * mm, "end": v(120.18, -388.4) * mm});
            skLineSegment(sketch, "E54.0.6.5", {"start": v(-690.3, -192.15) * mm, "end": v(-578.29, -386.15) * mm});
            skLineSegment(sketch, "E54.0.6.6", {"start": v(-917.77, -190.15) * mm, "end": v(-805.77, -384.15) * mm});
            skLineSegment(sketch, "E54.0.6.7", {"start": v(-805.77, -384.15) * mm, "end": v(-693.76, -190.15) * mm});
            skLineSegment(sketch, "E54.0.6.8", {"start": v(-117.25, -386.15) * mm, "end": v(-341.26, -386.15) * mm});
            skLineSegment(sketch, "E54.0.6.9", {"start": v(351.11, -389.9) * mm, "end": v(464.37, -196.62) * mm});
            skLineSegment(sketch, "E54.0.6.10", {"start": v(-344.3, -384.9) * mm, "end": v(-231.88, -191.13) * mm});
            skLineSegment(sketch, "E54.0.6.11", {"start": v(-1033.24, -386.15) * mm, "end": v(-809.23, -386.15) * mm});
            skLineSegment(sketch, "E54.0.6.12", {"start": v(467.85, -194.64) * mm, "end": v(578.6, -389.36) * mm});
            skLineSegment(sketch, "E54.0.6.13", {"start": v(-0.95, -192.12) * mm, "end": v(-113.8, -385.64) * mm});
            skLineSegment(sketch, "E54.0.6.14", {"start": v(-686.84, -190.16) * mm, "end": v(-462.82, -190.64) * mm});
            skLineSegment(sketch, "E54.0.6.15", {"start": v(-693.76, -190.15) * mm, "end": v(-917.77, -190.15) * mm});
            skLineSegment(sketch, "E54.0.6.16", {"start": v(-924.7, -190.15) * mm, "end": v(-1036.7, -384.15) * mm});
            skLineSegment(sketch, "E54.0.6.17", {"start": v(344.19, -389.85) * mm, "end": v(233.43, -195.13) * mm});
            skLineSegment(sketch, "E54.0.6.18", {"start": v(-572.2, -386.15) * mm, "end": v(-348.2, -386.15) * mm});
            skLineSegment(sketch, "E54.0.6.19", {"start": v(-1148.71, -190.15) * mm, "end": v(-924.7, -190.15) * mm});
            skLineSegment(sketch, "E54.0.6.20", {"start": v(-1036.7, -384.15) * mm, "end": v(-1148.71, -190.15) * mm});
            skLineSegment(sketch, "E54.0.6.21", {"start": v(-578.29, -386.15) * mm, "end": v(-802.3, -386.15) * mm});
            skLineSegment(sketch, "E54.0.6.22", {"start": v(5.98, -192.15) * mm, "end": v(117.15, -386.63) * mm});
            skLineSegment(sketch, "E54.0.6.23", {"start": v(575.12, -391.34) * mm, "end": v(351.11, -389.9) * mm});
            skLineSegment(sketch, "E54.0.6.24", {"start": v(-113.8, -385.64) * mm, "end": v(-224.96, -191.16) * mm});
            skLineSegment(sketch, "E54.0.6.25", {"start": v(-921.24, -192.15) * mm, "end": v(-1033.24, -386.15) * mm});
            skLineSegment(sketch, "E54.0.6.26", {"start": v(-109.91, -386.92) * mm, "end": v(3.34, -193.64) * mm});
            skLineSegment(sketch, "E54.0.6.27", {"start": v(691.85, -196.09) * mm, "end": v(467.85, -194.64) * mm});
            skLineSegment(sketch, "E54.0.6.28", {"start": v(-575.25, -384.4) * mm, "end": v(-686.84, -190.16) * mm});
            skLineSegment(sketch, "E54.0.6.29", {"start": v(-460.2, -192.15) * mm, "end": v(-572.2, -386.15) * mm});
            skLineSegment(sketch, "E54.0.6.30", {"start": v(120.18, -388.4) * mm, "end": v(344.19, -389.85) * mm});
            skLineSegment(sketch, "E54.0.6.31", {"start": v(114.1, -388.36) * mm, "end": v(-109.91, -386.92) * mm});
            skLineSegment(sketch, "E54.0.6.32", {"start": v(578.6, -389.36) * mm, "end": v(691.85, -196.09) * mm});
            skLineSegment(sketch, "E54.0.6.33", {"start": v(117.15, -386.63) * mm, "end": v(229.99, -193.11) * mm});
            skPoint(sketch, "E54.0.6.34", {"position": v(-978.97, -288.15) * mm});
            skLineSegment(sketch, "E54.0.6.35", {"start": v(-802.3, -386.15) * mm, "end": v(-690.3, -192.15) * mm});
            skLineSegment(sketch, "E54.0.6.36", {"start": v(460.92, -194.6) * mm, "end": v(347.66, -387.87) * mm});
            skLineSegment(sketch, "E54.0.6.37", {"start": v(-341.26, -386.15) * mm, "end": v(-229.26, -192.15) * mm});
            skLineSegment(sketch, "E54.0.6.38", {"start": v(-231.88, -191.13) * mm, "end": v(-455.9, -190.65) * mm});
            skLineSegment(sketch, "E54.0.6.39", {"start": v(578.6, -389.36) * mm, "end": v(579.85, -195.36) * mm, "construction": true});
            skLineSegment(sketch, "E54.0.6.40", {"start": v(3.34, -193.64) * mm, "end": v(114.1, -388.36) * mm});
            skLineSegment(sketch, "E54.0.6.41", {"start": v(464.37, -196.62) * mm, "end": v(575.12, -391.34) * mm});
            skLineSegment(sketch, "E54.0.6.42", {"start": v(-224.96, -191.16) * mm, "end": v(-0.95, -192.12) * mm});
            skLineSegment(sketch, "E54.0.6.43", {"start": v(-809.23, -386.15) * mm, "end": v(-921.24, -192.15) * mm});
            skLineSegment(sketch, "E54.0.6.44", {"start": v(236.91, -193.15) * mm, "end": v(460.92, -194.6) * mm});
            skLineSegment(sketch, "E54.0.6.45", {"start": v(-229.26, -192.15) * mm, "end": v(-117.25, -386.15) * mm});
            skLineSegment(sketch, "E54.0.6.46", {"start": v(-455.9, -190.65) * mm, "end": v(-344.3, -384.9) * mm});
            skLineSegment(sketch, "E54.0.7.0", {"start": v(229.99, -393.11) * mm, "end": v(5.98, -392.15) * mm});
            skLineSegment(sketch, "E54.0.7.1", {"start": v(-462.82, -390.64) * mm, "end": v(-575.25, -584.4) * mm});
            skLineSegment(sketch, "E54.0.7.2", {"start": v(-348.2, -586.15) * mm, "end": v(-460.2, -392.15) * mm});
            skLineSegment(sketch, "E54.0.7.3", {"start": v(347.66, -587.87) * mm, "end": v(236.91, -393.15) * mm});
            skLineSegment(sketch, "E54.0.7.4", {"start": v(233.43, -395.13) * mm, "end": v(120.18, -588.4) * mm});
            skLineSegment(sketch, "E54.0.7.5", {"start": v(-690.3, -392.15) * mm, "end": v(-578.29, -586.15) * mm});
            skLineSegment(sketch, "E54.0.7.6", {"start": v(-917.77, -390.15) * mm, "end": v(-805.77, -584.15) * mm});
            skLineSegment(sketch, "E54.0.7.7", {"start": v(-805.77, -584.15) * mm, "end": v(-693.76, -390.15) * mm});
            skLineSegment(sketch, "E54.0.7.8", {"start": v(-117.25, -586.15) * mm, "end": v(-341.26, -586.15) * mm});
            skLineSegment(sketch, "E54.0.7.9", {"start": v(351.11, -589.9) * mm, "end": v(464.37, -396.62) * mm});
            skLineSegment(sketch, "E54.0.7.10", {"start": v(-344.3, -584.9) * mm, "end": v(-231.88, -391.13) * mm});
            skLineSegment(sketch, "E54.0.7.11", {"start": v(-1033.24, -586.15) * mm, "end": v(-809.23, -586.15) * mm});
            skLineSegment(sketch, "E54.0.7.12", {"start": v(467.85, -394.64) * mm, "end": v(578.6, -589.36) * mm});
            skLineSegment(sketch, "E54.0.7.13", {"start": v(-0.95, -392.12) * mm, "end": v(-113.8, -585.64) * mm});
            skLineSegment(sketch, "E54.0.7.14", {"start": v(-686.84, -390.16) * mm, "end": v(-462.82, -390.64) * mm});
            skLineSegment(sketch, "E54.0.7.15", {"start": v(-693.76, -390.15) * mm, "end": v(-917.77, -390.15) * mm});
            skLineSegment(sketch, "E54.0.7.16", {"start": v(-924.7, -390.15) * mm, "end": v(-1036.7, -584.15) * mm});
            skLineSegment(sketch, "E54.0.7.17", {"start": v(344.19, -589.85) * mm, "end": v(233.43, -395.13) * mm});
            skLineSegment(sketch, "E54.0.7.18", {"start": v(-572.2, -586.15) * mm, "end": v(-348.2, -586.15) * mm});
            skLineSegment(sketch, "E54.0.7.19", {"start": v(-1148.71, -390.15) * mm, "end": v(-924.7, -390.15) * mm});
            skLineSegment(sketch, "E54.0.7.20", {"start": v(-1036.7, -584.15) * mm, "end": v(-1148.71, -390.15) * mm});
            skLineSegment(sketch, "E54.0.7.21", {"start": v(-578.29, -586.15) * mm, "end": v(-802.3, -586.15) * mm});
            skLineSegment(sketch, "E54.0.7.22", {"start": v(5.98, -392.15) * mm, "end": v(117.15, -586.63) * mm});
            skLineSegment(sketch, "E54.0.7.23", {"start": v(575.12, -591.34) * mm, "end": v(351.11, -589.9) * mm});
            skLineSegment(sketch, "E54.0.7.24", {"start": v(-113.8, -585.64) * mm, "end": v(-224.96, -391.16) * mm});
            skLineSegment(sketch, "E54.0.7.25", {"start": v(-921.24, -392.15) * mm, "end": v(-1033.24, -586.15) * mm});
            skLineSegment(sketch, "E54.0.7.26", {"start": v(-109.91, -586.92) * mm, "end": v(3.34, -393.64) * mm});
            skLineSegment(sketch, "E54.0.7.27", {"start": v(691.85, -396.09) * mm, "end": v(467.85, -394.64) * mm});
            skLineSegment(sketch, "E54.0.7.28", {"start": v(-575.25, -584.4) * mm, "end": v(-686.84, -390.16) * mm});
            skLineSegment(sketch, "E54.0.7.29", {"start": v(-460.2, -392.15) * mm, "end": v(-572.2, -586.15) * mm});
            skLineSegment(sketch, "E54.0.7.30", {"start": v(120.18, -588.4) * mm, "end": v(344.19, -589.85) * mm});
            skLineSegment(sketch, "E54.0.7.31", {"start": v(114.1, -588.36) * mm, "end": v(-109.91, -586.92) * mm});
            skLineSegment(sketch, "E54.0.7.32", {"start": v(578.6, -589.36) * mm, "end": v(691.85, -396.09) * mm});
            skLineSegment(sketch, "E54.0.7.33", {"start": v(117.15, -586.63) * mm, "end": v(229.99, -393.11) * mm});
            skPoint(sketch, "E54.0.7.34", {"position": v(-978.97, -488.15) * mm});
            skLineSegment(sketch, "E54.0.7.35", {"start": v(-802.3, -586.15) * mm, "end": v(-690.3, -392.15) * mm});
            skLineSegment(sketch, "E54.0.7.36", {"start": v(460.92, -394.6) * mm, "end": v(347.66, -587.87) * mm});
            skLineSegment(sketch, "E54.0.7.37", {"start": v(-341.26, -586.15) * mm, "end": v(-229.26, -392.15) * mm});
            skLineSegment(sketch, "E54.0.7.38", {"start": v(-231.88, -391.13) * mm, "end": v(-455.9, -390.65) * mm});
            skLineSegment(sketch, "E54.0.7.39", {"start": v(578.6, -589.36) * mm, "end": v(579.85, -395.36) * mm, "construction": true});
            skLineSegment(sketch, "E54.0.7.40", {"start": v(3.34, -393.64) * mm, "end": v(114.1, -588.36) * mm});
            skLineSegment(sketch, "E54.0.7.41", {"start": v(464.37, -396.62) * mm, "end": v(575.12, -591.34) * mm});
            skLineSegment(sketch, "E54.0.7.42", {"start": v(-224.96, -391.16) * mm, "end": v(-0.95, -392.12) * mm});
            skLineSegment(sketch, "E54.0.7.43", {"start": v(-809.23, -586.15) * mm, "end": v(-921.24, -392.15) * mm});
            skLineSegment(sketch, "E54.0.7.44", {"start": v(236.91, -393.15) * mm, "end": v(460.92, -394.6) * mm});
            skLineSegment(sketch, "E54.0.7.45", {"start": v(-229.26, -392.15) * mm, "end": v(-117.25, -586.15) * mm});
            skLineSegment(sketch, "E54.0.7.46", {"start": v(-455.9, -390.65) * mm, "end": v(-344.3, -584.9) * mm});
            skLineSegment(sketch, "E54.direction1", {"start": v(5.98, 1007.85) * mm, "end": v(30.98, 1007.85) * mm, "construction": true});
            skLineSegment(sketch, "E54.direction2", {"start": v(5.98, 1007.85) * mm, "end": v(5.98, 807.85) * mm, "construction": true});
            skSolve(sketch);
        }
        {
            var Q0;
            Q0 = qSketchRegion(id + "F0", true);
            extrude(context, id + "F1", {"entities" : qUnion([Q0]), "depth" : 5 * mm});
        }
    });
